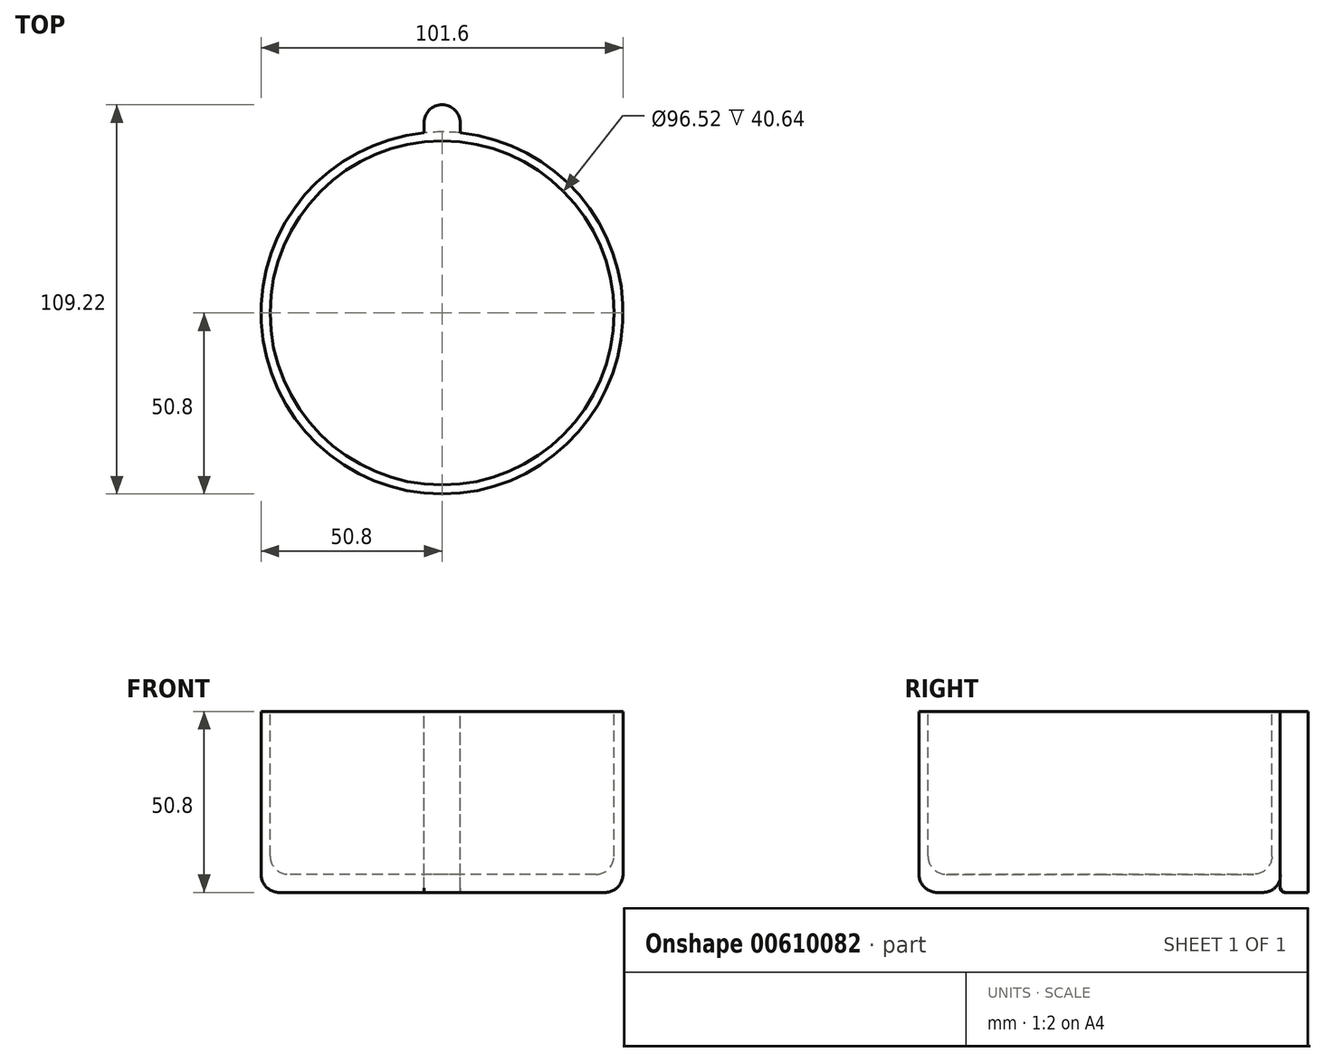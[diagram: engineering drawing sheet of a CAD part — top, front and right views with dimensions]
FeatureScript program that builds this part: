
annotation { "Feature Type Name" : "Feature", "Feature Type Description" : "" }
export const myFeature = defineFeature(function(context is Context, id is Id, definition is map)
    precondition{}
    {
        {
            var Q0;
            Q0=qCreatedBy(makeId("Top.planeOp"),FACE);
            var sketch = newSketch(context, id + "F0", { "sketchPlane" : qUnion([Q0])});
            skCircle(sketch, "E0", {"center": v(0, 0) * mm, "radius": 50.8 * mm});
            skSolve(sketch);
        }
        {
            var Q0;
            Q0=makeQuery(id+"F0.imprint","IMPRINT",FACE,{"disambiguationData":[TD([[makeQuery(id+"F0.imprint","IMPRINT",EDGE,{"derivedFrom":sQuery(id+"F0.wireOp",EDGE,"E0")}),1.0]])]});
            extrude(context, id + "F1", {"entities" : qUnion([Q0]), "depth" : 50.8 * mm, "offsetDistance" : 25.4 * mm});
        }
        {
            var Q0;
            Q0=makeQuery(id+"F1.opExtrude","CAP_FACE",FACE,{"disambiguationData":[OSD([sQuery(id+"F0.wireOp",EDGE,"E0")])],"isStart":false});
            var sketch = newSketch(context, id + "F2", { "sketchPlane" : qUnion([Q0])});
            skCircle(sketch, "E1", {"center": v(0, 0) * mm, "radius": 48.26 * mm});
            skSolve(sketch);
        }
        {
            var Q0;
            Q0 = qSketchRegion(id + "F2", true);
            extrude(context, id + "F3", {"entities" : qUnion([Q0]), "operationType" : NewBodyOperationType.REMOVE, "oppositeDirection" : true, "depth" : 45.72 * mm, "offsetDistance" : 25.4 * mm});
        }
        {
            var Q0;
            Q0=makeQuery(id+"F3.boolean.opBoolean","COPY",EDGE,{"derivedFrom":makeQuery(id+"F3.opExtrude","CAP_EDGE",EDGE,{"disambiguationData":[OSD([sQuery(id+"F2.wireOp",EDGE,"E1")])],"isStart":false})});
            fillet(context, id + "F4", {"entities" : qUnion([Q0]), "radius" : 5.08 * mm, "tangentPropagation" : true, "allowEdgeOverflow" : false});
        }
        {
            var Q0;
            Q0=makeQuery(id+"F1.opExtrude","CAP_EDGE",EDGE,{"disambiguationData":[OSD([sQuery(id+"F0.wireOp",EDGE,"E0")])],"isStart":true});
            fillet(context, id + "F5", {"entities" : qUnion([Q0]), "radius" : 5.08 * mm, "tangentPropagation" : true, "allowEdgeOverflow" : false});
        }
        {
            var Q0;
            Q0=makeQuery(id+"F1.opExtrude","CAP_FACE",FACE,{"disambiguationData":[OSD([sQuery(id+"F0.wireOp",EDGE,"E0")])],"isStart":false});
            var sketch = newSketch(context, id + "F6", { "sketchPlane" : qUnion([Q0])});
            skLineSegment(sketch, "E2", {"start": v(-5.08, 50.8) * mm, "end": v(-5.08, 53.34) * mm});
            skLineSegment(sketch, "E3", {"start": v(-5.08, 53.34) * mm, "end": v(-5.08, 50.54) * mm});
            skLineSegment(sketch, "E4", {"start": v(5.08, 50.8) * mm, "end": v(5.08, 53.34) * mm});
            skArc(sketch, "E5", {"start": v(5.08, 53.34) * mm, "mid": v(0, 58.42) * mm, "end": v(-5.08, 53.34) * mm});
            skLineSegment(sketch, "E6", {"start": v(5.08, 50.8) * mm, "end": v(5.08, 50.55) * mm});
            skSolve(sketch);
        }
        {
            var Q0;
            {var subQ0=sQuery(id+"F6.wireOp",EDGE,"E3");Q0=makeQuery(id+"F6.imprint","IMPRINT",FACE,{"disambiguationData":[TD([[makeQuery(id+"F6.imprint","IMPRINT",EDGE,{"derivedFrom":subQ0}),1.0]])]});}
            extrude(context, id + "F7", {"entities" : qUnion([Q0]), "operationType" : NewBodyOperationType.ADD, "oppositeDirection" : true, "depth" : 50.8 * mm, "offsetDistance" : 25.4 * mm});
        }
        {
            var Q0;
            Q0=makeQuery(id+"F7.opExtrude","CAP_EDGE",EDGE,{"disambiguationData":[OSD([sQuery(id+"F0.wireOp",EDGE,"E0")])],"isStart":false});
            fillet(context, id + "F8", {"entities" : qUnion([Q0]), "radius" : 1.27 * mm, "tangentPropagation" : true, "allowEdgeOverflow" : false});
        }
        {
            var Q0;
            Q0=qCreatedBy(makeId("Right.planeOp"),FACE);
            var sketch = newSketch(context, id + "F9", { "sketchPlane" : qUnion([Q0])});
            skLineSegment(sketch, "E7", {"start": v(54.52, 53.34) * mm, "end": v(57.55, 53.34) * mm});
            skLineSegment(sketch, "E8", {"start": v(57.55, 53.34) * mm, "end": v(54.52, 0) * mm});
            skLineSegment(sketch, "E9", {"start": v(54.52, 0) * mm, "end": v(54.52, 53.34) * mm});
            skSolve(sketch);
        }
        {
            var Q0;
            Q0 = qSketchRegion(id + "F9", true);
            var Q1;
            Q1=sQuery(id+"F9.wireOp",EDGE,"E7");
            var Q2;
            Q2=sQuery(id+"F9.wireOp",EDGE,"E8");
            var Q3;
            Q3=sQuery(id+"F9.wireOp",EDGE,"E9");
            revolve(context, id + "F10", {"bodyType" : ToolBodyType.SURFACE, "operationType" : NewBodyOperationType.ADD, "entities" : qUnion([Q0]), "surfaceEntities" : qUnion([Q1, Q2]), "axis" : qUnion([Q3]), "revolveType" : RevolveType.FULL, "oppositeDirection" : true});
        }
    });
